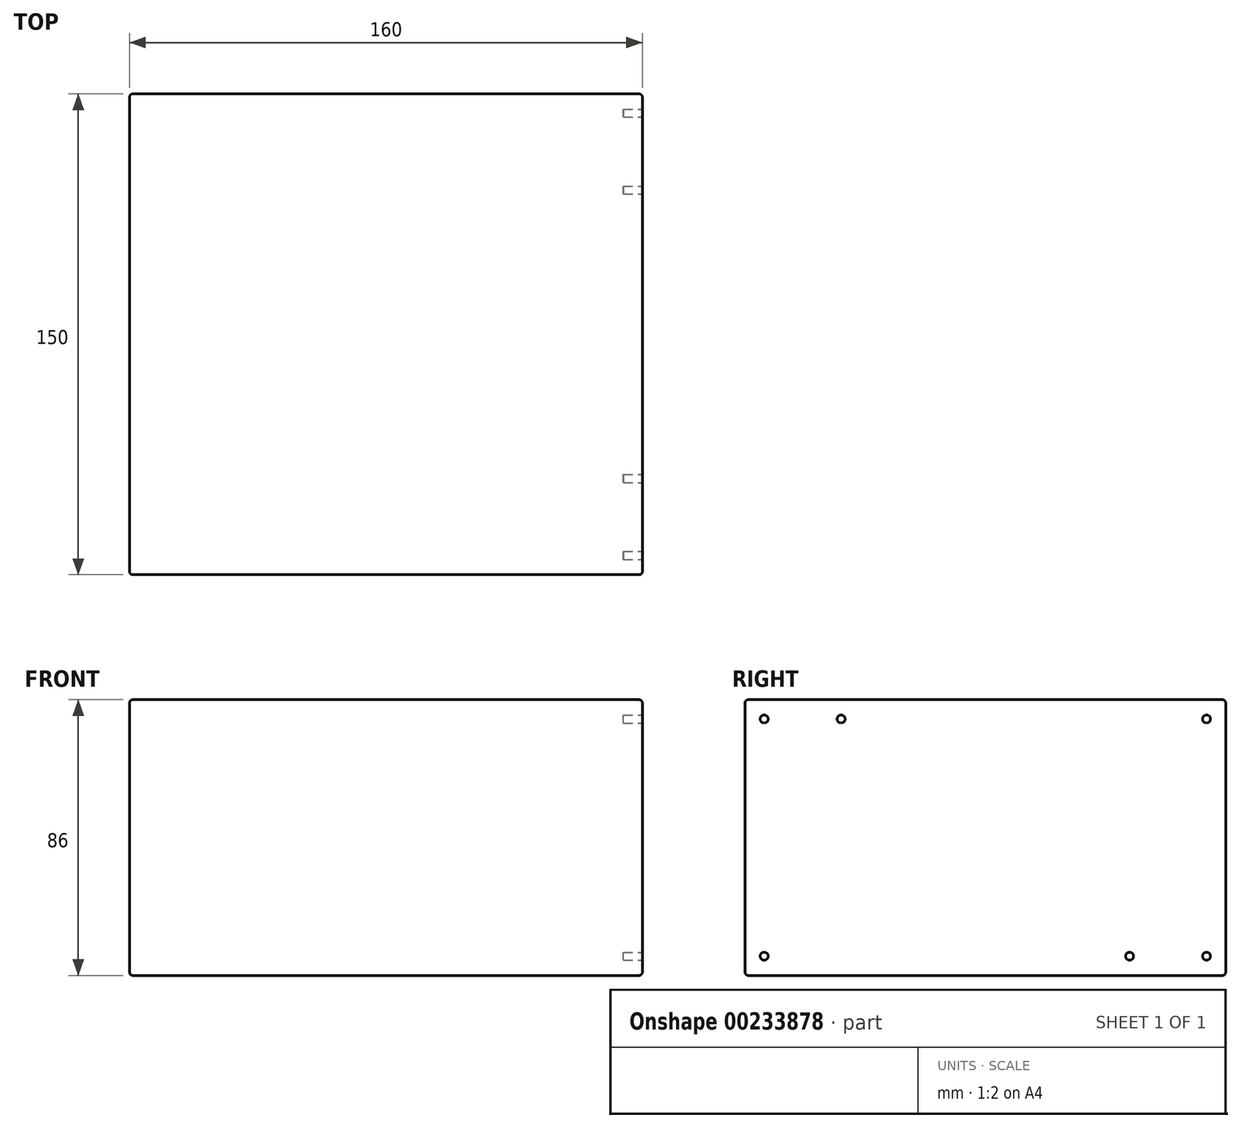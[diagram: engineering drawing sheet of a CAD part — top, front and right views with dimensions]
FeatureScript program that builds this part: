
annotation { "Feature Type Name" : "Feature", "Feature Type Description" : "" }
export const myFeature = defineFeature(function(context is Context, id is Id, definition is map)
    precondition{}
    {
        {
            var Q0;
            Q0=qCreatedBy(makeId("Top.planeOp"),FACE);
            var sketch = newSketch(context, id + "F0", { "sketchPlane" : qUnion([Q0])});
            skLineSegment(sketch, "E0.bottom", {"start": v(0, 0) * mm, "end": v(160, 0) * mm});
            skLineSegment(sketch, "E0.top", {"start": v(0, 150) * mm, "end": v(160, 150) * mm});
            skLineSegment(sketch, "E0.left", {"start": v(0, 0) * mm, "end": v(0, 150) * mm});
            skLineSegment(sketch, "E0.right", {"start": v(160, 0) * mm, "end": v(160, 150) * mm});
            skSolve(sketch);
        }
        {
            var Q0;
            Q0 = qSketchRegion(id + "F0", true);
            extrude(context, id + "F1", {"entities" : qUnion([Q0]), "depth" : 86 * mm});
        }
        {
            var Q0;
            Q0=makeQuery(id+"F1.opExtrude","SWEPT_FACE",FACE,{"disambiguationData":[OSD([sQuery(id+"F0.wireOp",EDGE,"E0.right")])]});
            var sketch = newSketch(context, id + "F2", { "sketchPlane" : qUnion([Q0])});
            skCircle(sketch, "E1", {"center": v(6, 80) * mm, "radius": 1.25 * mm});
            skCircle(sketch, "E2", {"center": v(30, 80) * mm, "radius": 1.25 * mm});
            skCircle(sketch, "E3", {"center": v(144, 80) * mm, "radius": 1.25 * mm});
            skCircle(sketch, "E4", {"center": v(144, 6) * mm, "radius": 1.25 * mm});
            skCircle(sketch, "E5", {"center": v(6, 6) * mm, "radius": 1.25 * mm});
            skCircle(sketch, "E6", {"center": v(120, 6) * mm, "radius": 1.25 * mm});
            skLineSegment(sketch, "E7", {"start": v(144, 80) * mm, "end": v(150, 80) * mm, "construction": true});
            skLineSegment(sketch, "E8", {"start": v(144, 80) * mm, "end": v(144, 86) * mm, "construction": true});
            skLineSegment(sketch, "E9", {"start": v(6, 6) * mm, "end": v(6, 0) * mm, "construction": true});
            skSolve(sketch);
        }
        {
            var Q0;
            Q0 = qSketchRegion(id + "F2", true);
            extrude(context, id + "F3", {"entities" : qUnion([Q0]), "operationType" : NewBodyOperationType.REMOVE, "oppositeDirection" : true, "depth" : 6 * mm});
        }
        {
            var Q0;
            Q0=makeQuery(id+"F1.opExtrude","CAP_EDGE",EDGE,{"disambiguationData":[OSD([sQuery(id+"F0.wireOp",EDGE,"E0.right")])],"isStart":false});
            var Q1;
            Q1=makeQuery(id+"F1.opExtrude","CAP_EDGE",EDGE,{"disambiguationData":[OSD([sQuery(id+"F0.wireOp",EDGE,"E0.bottom")])],"isStart":false});
            var Q2;
            Q2=makeQuery(id+"F1.opExtrude","SWEPT_EDGE",EDGE,{"disambiguationData":[OSD([sQuery(id+"F0.wireOp",EDGE,"E0.bottom"),sQuery(id+"F0.wireOp",EDGE,"E0.right")])]});
            var Q3;
            Q3=makeQuery(id+"F1.opExtrude","CAP_EDGE",EDGE,{"disambiguationData":[OSD([sQuery(id+"F0.wireOp",EDGE,"E0.top")])],"isStart":false});
            var Q4;
            Q4=makeQuery(id+"F1.opExtrude","CAP_EDGE",EDGE,{"disambiguationData":[OSD([sQuery(id+"F0.wireOp",EDGE,"E0.left")])],"isStart":false});
            var Q5;
            Q5=makeQuery(id+"F1.opExtrude","CAP_EDGE",EDGE,{"disambiguationData":[OSD([sQuery(id+"F0.wireOp",EDGE,"E0.bottom")])],"isStart":true});
            var Q6;
            Q6=makeQuery(id+"F1.opExtrude","SWEPT_EDGE",EDGE,{"disambiguationData":[OSD([sQuery(id+"F0.wireOp",EDGE,"E0.bottom"),sQuery(id+"F0.wireOp",EDGE,"E0.left")])]});
            var Q7;
            Q7=makeQuery(id+"F1.opExtrude","CAP_EDGE",EDGE,{"disambiguationData":[OSD([sQuery(id+"F0.wireOp",EDGE,"E0.right")])],"isStart":true});
            var Q8;
            Q8=makeQuery(id+"F1.opExtrude","SWEPT_EDGE",EDGE,{"disambiguationData":[OSD([sQuery(id+"F0.wireOp",EDGE,"E0.top"),sQuery(id+"F0.wireOp",EDGE,"E0.right")])]});
            var Q9;
            Q9=makeQuery(id+"F1.opExtrude","CAP_EDGE",EDGE,{"disambiguationData":[OSD([sQuery(id+"F0.wireOp",EDGE,"E0.top")])],"isStart":true});
            var Q10;
            Q10=makeQuery(id+"F1.opExtrude","CAP_EDGE",EDGE,{"disambiguationData":[OSD([sQuery(id+"F0.wireOp",EDGE,"E0.left")])],"isStart":true});
            var Q11;
            Q11=makeQuery(id+"F1.opExtrude","SWEPT_EDGE",EDGE,{"disambiguationData":[OSD([sQuery(id+"F0.wireOp",EDGE,"E0.top"),sQuery(id+"F0.wireOp",EDGE,"E0.left")])]});
            fillet(context, id + "F4", {"entities" : qUnion([Q0, Q1, Q2, Q3, Q4, Q5, Q6, Q7, Q8, Q9, Q10, Q11]), "radius" : 1 * mm, "tangentPropagation" : true, "allowEdgeOverflow" : false});
        }
    });
